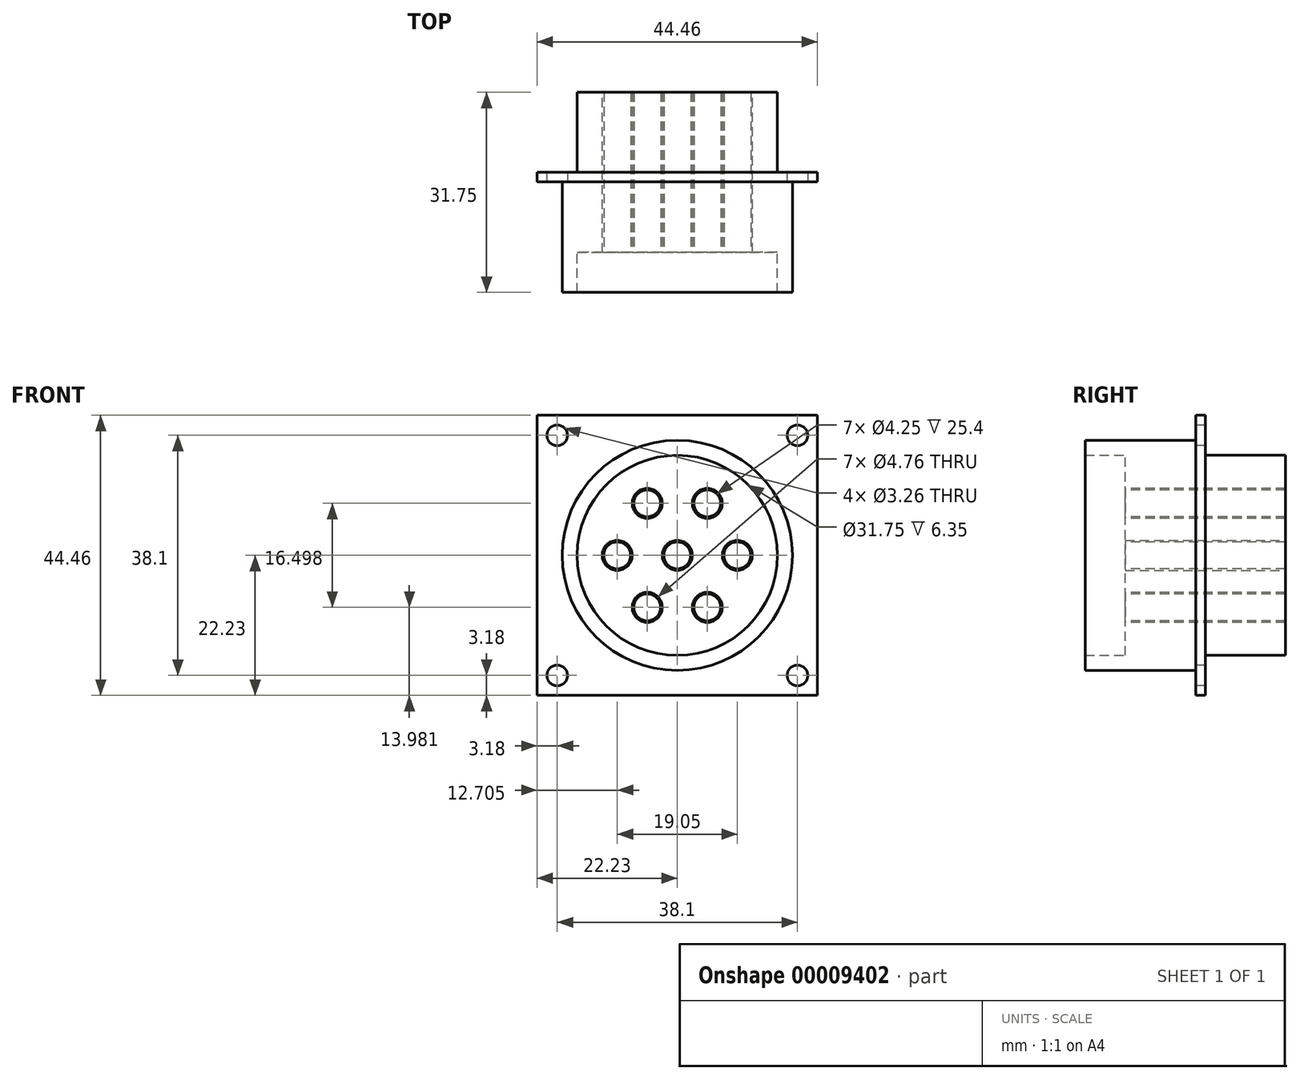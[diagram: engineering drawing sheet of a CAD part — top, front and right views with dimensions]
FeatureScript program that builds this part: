
annotation { "Feature Type Name" : "Feature", "Feature Type Description" : "" }
export const myFeature = defineFeature(function(context is Context, id is Id, definition is map)
    precondition{}
    {
        {
            var Q0;
            Q0=qCreatedBy(makeId("Front.planeOp"),FACE);
            var sketch = newSketch(context, id + "F0", { "sketchPlane" : qUnion([Q0])});
            skLineSegment(sketch, "E0.bottom", {"start": v(22.22, 22.22) * mm, "end": v(-22.23, 22.22) * mm});
            skLineSegment(sketch, "E0.top", {"start": v(22.22, -22.23) * mm, "end": v(-22.23, -22.23) * mm});
            skLineSegment(sketch, "E0.left", {"start": v(22.22, 22.22) * mm, "end": v(22.22, -22.23) * mm});
            skLineSegment(sketch, "E0.right", {"start": v(-22.23, 22.22) * mm, "end": v(-22.23, -22.23) * mm});
            skPoint(sketch, "E0.middle", {"position": v(0, 0) * mm});
            skLineSegment(sketch, "E1.bottom", {"start": v(19.05, 19.05) * mm, "end": v(-19.05, 19.05) * mm});
            skLineSegment(sketch, "E1.top", {"start": v(19.05, -19.05) * mm, "end": v(-19.05, -19.05) * mm});
            skLineSegment(sketch, "E1.left", {"start": v(19.05, 19.05) * mm, "end": v(19.05, -19.05) * mm});
            skLineSegment(sketch, "E1.right", {"start": v(-19.05, 19.05) * mm, "end": v(-19.05, -19.05) * mm});
            skCircle(sketch, "E2", {"center": v(0, 0) * mm, "radius": 18.26 * mm});
            skCircle(sketch, "E3", {"center": v(0, 0) * mm, "radius": 15.88 * mm});
            skSolve(sketch);
        }
        {
            var Q0;
            Q0=makeQuery(id+"F0.imprint","IMPRINT",FACE,{"disambiguationData":[TD([[makeQuery(id+"F0.imprint","IMPRINT",EDGE,{"derivedFrom":sQuery(id+"F0.wireOp",EDGE,"E0.bottom")}),1.0]])]});
            var Q1;
            Q1=makeQuery(id+"F0.imprint","IMPRINT",FACE,{"disambiguationData":[TD([[makeQuery(id+"F0.imprint","IMPRINT",EDGE,{"derivedFrom":sQuery(id+"F0.wireOp",EDGE,"E1.bottom")}),1.0]])]});
            extrude(context, id + "F1", {"entities" : qUnion([Q0, Q1]), "depth" : 1.52 * mm, "offsetDistance" : 25.4 * mm});
        }
        {
            var Q0;
            Q0=makeQuery(id+"F0.imprint","IMPRINT",FACE,{"disambiguationData":[TD([[makeQuery(id+"F0.imprint","IMPRINT",EDGE,{"derivedFrom":sQuery(id+"F0.wireOp",EDGE,"E2")}),1.0]])]});
            extrude(context, id + "F2", {"entities" : qUnion([Q0]), "operationType" : NewBodyOperationType.ADD, "depth" : 19.05 * mm, "offsetDistance" : 25.4 * mm});
        }
        {
            var Q0;
            Q0=sQuery(id+"F0.wireOp",VERTEX,"E1.bottom.start");
            var Q1;
            Q1=sQuery(id+"F0.wireOp",VERTEX,"E1.bottom.end");
            var Q2;
            Q2=sQuery(id+"F0.wireOp",VERTEX,"E1.top.end");
            var Q3;
            Q3=sQuery(id+"F0.wireOp",VERTEX,"E1.top.start");
            var Q4;
            Q4=makeQuery(id+"F1.opExtrude","SWEPT_BODY",BODY,{"disambiguationData":[OSD([sQuery(id+"F0.wireOp",EDGE,"E0.bottom"),sQuery(id+"F0.wireOp",EDGE,"E0.top"),sQuery(id+"F0.wireOp",EDGE,"E0.left"),sQuery(id+"F0.wireOp",EDGE,"E0.right"),sQuery(id+"F0.wireOp",EDGE,"E2")])]});
            hole(context, id + "F3", {"style" : HoleStyle.SIMPLE, "endStyle" : HoleEndStyle.THROUGH, "oppositeDirection" : true, "standardTappedOrClearance" : lookupTablePath({ "fit" : "Free", "standard" : "ANSI", "size" : "#4", "type" : "Clearance" }), "standardBlindInLast" : lookupTablePath({ "fit" : "Free", "standard" : "ANSI", "engagement" : "75%", "pitch" : "40 tpi", "size" : "#4", "type" : "Clearance & tapped" }), "holeDiameter" : 3.26 * mm, "majorDiameter" : 6.35 * mm, "isTappedThrough" : true, "tappedDepth" : 12.7 * mm, "tapClearance" : 3, "startFromSketch" : true, "locations" : qUnion([Q0, Q1, Q2, Q3]), "scope" : qUnion([Q4])});
        }
        {
            var Q0;
            Q0=makeQuery(id+"F0.imprint","IMPRINT",FACE,{"disambiguationData":[TD([[makeQuery(id+"F0.imprint","IMPRINT",EDGE,{"derivedFrom":sQuery(id+"F0.wireOp",EDGE,"E3")}),1.0]])]});
            extrude(context, id + "F4", {"entities" : qUnion([Q0]), "operationType" : NewBodyOperationType.ADD, "depth" : 25.4 * mm, "offsetDistance" : 25.4 * mm, "symmetric" : true});
        }
        {
            var Q0;
            Q0=makeQuery(id+"F4.opExtrude","CAP_FACE",FACE,{"disambiguationData":[OSD([sQuery(id+"F0.wireOp",EDGE,"E3")])],"isStart":false});
            var sketch = newSketch(context, id + "F5", { "sketchPlane" : qUnion([Q0])});
            skPoint(sketch, "E4.0", {"position": v(0, 0) * mm});
            skPoint(sketch, "E5", {"position": v(-9.53, 0) * mm});
            skPoint(sketch, "E6.1.0", {"position": v(-4.76, -8.25) * mm});
            skPoint(sketch, "E6.2.0", {"position": v(4.76, -8.25) * mm});
            skPoint(sketch, "E7.0.3.0", {"position": v(9.53, 0) * mm});
            skPoint(sketch, "E7.0.4.0", {"position": v(4.76, 8.25) * mm});
            skPoint(sketch, "E7.0.5.0", {"position": v(-4.76, 8.25) * mm});
            skSolve(sketch);
        }
        {
            var Q0;
            Q0=sQuery(id+"F5.wireOp",VERTEX,"E5");
            var Q1;
            Q1=sQuery(id+"F5.wireOp",VERTEX,"E7.0.5.0");
            var Q2;
            Q2=sQuery(id+"F5.wireOp",VERTEX,"E7.0.4.0");
            var Q3;
            Q3=sQuery(id+"F5.wireOp",VERTEX,"E7.0.3.0");
            var Q4;
            Q4=sQuery(id+"F5.wireOp",VERTEX,"E4.0");
            var Q5;
            Q5=sQuery(id+"F5.wireOp",VERTEX,"E6.2.0");
            var Q6;
            Q6=sQuery(id+"F5.wireOp",VERTEX,"E6.1.0");
            var Q7;
            Q7=makeQuery(id+"F1.opExtrude","SWEPT_BODY",BODY,{"disambiguationData":[OSD([sQuery(id+"F0.wireOp",EDGE,"E0.bottom"),sQuery(id+"F0.wireOp",EDGE,"E0.top"),sQuery(id+"F0.wireOp",EDGE,"E0.left"),sQuery(id+"F0.wireOp",EDGE,"E0.right"),sQuery(id+"F0.wireOp",EDGE,"E2")])]});
            hole(context, id + "F6", {"style" : HoleStyle.SIMPLE, "endStyle" : HoleEndStyle.THROUGH, "holeDiameter" : 4.76 * mm, "majorDiameter" : 6.35 * mm, "isTappedThrough" : true, "tappedDepth" : 12.7 * mm, "tapClearance" : 3, "startFromSketch" : true, "locations" : qUnion([Q0, Q1, Q2, Q3, Q4, Q5, Q6]), "scope" : qUnion([Q7])});
        }
        {
            var Q0;
            Q0=makeQuery(id+"F4.opExtrude","CAP_FACE",FACE,{"disambiguationData":[OSD([sQuery(id+"F0.wireOp",EDGE,"E3")])],"isStart":false});
            var sketch = newSketch(context, id + "F7", { "sketchPlane" : qUnion([Q0])});
            skCircle(sketch, "E8.0.0", {"center": v(0, 0) * mm, "radius": 15.88 * mm});
            skCircle(sketch, "E9.0", {"center": v(-9.53, 0) * mm, "radius": 2.13 * mm});
            skCircle(sketch, "E10.0", {"center": v(0, 0) * mm, "radius": 2.13 * mm});
            skCircle(sketch, "E11.1.0", {"center": v(-4.76, -8.25) * mm, "radius": 2.13 * mm});
            skCircle(sketch, "E11.2.0", {"center": v(4.76, -8.25) * mm, "radius": 2.13 * mm});
            skCircle(sketch, "E11.3.0", {"center": v(9.53, 0) * mm, "radius": 2.13 * mm});
            skCircle(sketch, "E11.4.0", {"center": v(4.76, 8.25) * mm, "radius": 2.13 * mm});
            skCircle(sketch, "E11.5.0", {"center": v(-4.76, 8.25) * mm, "radius": 2.13 * mm});
            skSolve(sketch);
        }
        {
            var Q0;
            Q0=makeQuery(id+"F7.imprint","IMPRINT",FACE,{"disambiguationData":[TD([[makeQuery(id+"F7.imprint","IMPRINT",EDGE,{"derivedFrom":sQuery(id+"F7.wireOp",EDGE,"E9.0")}),-1.0]])]});
            var Q1;
            Q1=makeQuery(id+"F7.imprint","IMPRINT",FACE,{"disambiguationData":[TD([[makeQuery(id+"F7.imprint","IMPRINT",EDGE,{"derivedFrom":sQuery(id+"F7.wireOp",EDGE,"E11.5.0")}),-1.0]])]});
            var Q2;
            Q2=makeQuery(id+"F7.imprint","IMPRINT",FACE,{"disambiguationData":[TD([[makeQuery(id+"F7.imprint","IMPRINT",EDGE,{"derivedFrom":sQuery(id+"F7.wireOp",EDGE,"E11.4.0")}),-1.0]])]});
            var Q3;
            Q3=makeQuery(id+"F7.imprint","IMPRINT",FACE,{"disambiguationData":[TD([[makeQuery(id+"F7.imprint","IMPRINT",EDGE,{"derivedFrom":sQuery(id+"F7.wireOp",EDGE,"E10.0")}),-1.0]])]});
            var Q4;
            Q4=makeQuery(id+"F7.imprint","IMPRINT",FACE,{"disambiguationData":[TD([[makeQuery(id+"F7.imprint","IMPRINT",EDGE,{"derivedFrom":sQuery(id+"F7.wireOp",EDGE,"E11.3.0")}),-1.0]])]});
            var Q5;
            Q5=makeQuery(id+"F7.imprint","IMPRINT",FACE,{"disambiguationData":[TD([[makeQuery(id+"F7.imprint","IMPRINT",EDGE,{"derivedFrom":sQuery(id+"F7.wireOp",EDGE,"E11.2.0")}),-1.0]])]});
            var Q6;
            Q6=makeQuery(id+"F7.imprint","IMPRINT",FACE,{"disambiguationData":[TD([[makeQuery(id+"F7.imprint","IMPRINT",EDGE,{"derivedFrom":sQuery(id+"F7.wireOp",EDGE,"E11.1.0")}),-1.0]])]});
            extrude(context, id + "F8", {"entities" : qUnion([Q0, Q1, Q2, Q3, Q4, Q5, Q6]), "oppositeDirection" : true, "depth" : 25.4 * mm, "offsetDistance" : 25.4 * mm});
        }
    });
